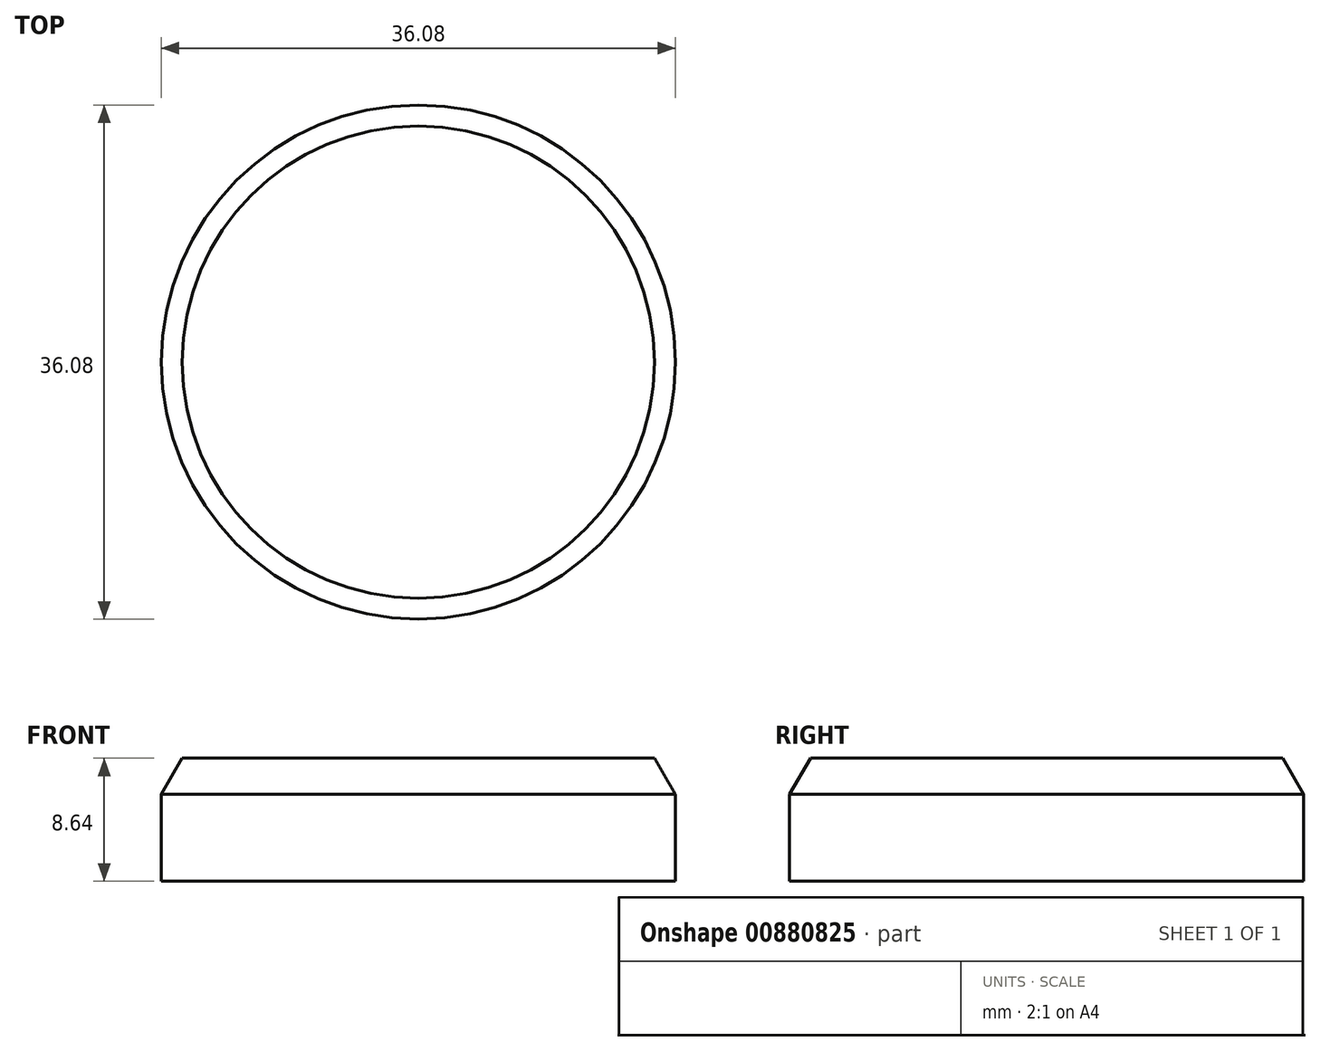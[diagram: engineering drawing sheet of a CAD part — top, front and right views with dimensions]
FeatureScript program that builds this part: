
annotation { "Feature Type Name" : "Feature", "Feature Type Description" : "" }
export const myFeature = defineFeature(function(context is Context, id is Id, definition is map)
    precondition{}
    {
        {
            var Q0;
            Q0=qCreatedBy(makeId("Top.planeOp"),FACE);
            var sketch = newSketch(context, id + "F0", { "sketchPlane" : qUnion([Q0])});
            skCircle(sketch, "E0", {"center": v(0, 0) * mm, "radius": 18.04 * mm});
            skSolve(sketch);
        }
        {
            var Q0;
            Q0=makeQuery(id+"F0.imprint","IMPRINT",FACE,{"disambiguationData":[TD([[makeQuery(id+"F0.imprint","IMPRINT",EDGE,{"derivedFrom":sQuery(id+"F0.wireOp",EDGE,"E0")}),1.0]])]});
            extrude(context, id + "F1", {"entities" : qUnion([Q0]), "depth" : 6.1 * mm, "offsetDistance" : 25.4 * mm});
        }
        {
            var Q0;
            Q0=makeQuery(id+"F1.opExtrude","CAP_FACE",FACE,{"disambiguationData":[OSD([sQuery(id+"F0.wireOp",EDGE,"E0")])],"isStart":false});
            extrude(context, id + "F2", {"entities" : qUnion([Q0]), "operationType" : NewBodyOperationType.ADD, "depth" : 2.54 * mm, "offsetDistance" : 25.4 * mm, "hasDraft" : true, "draftAngle" : 30 * degree, "draftPullDirection" : true});
        }
    });
